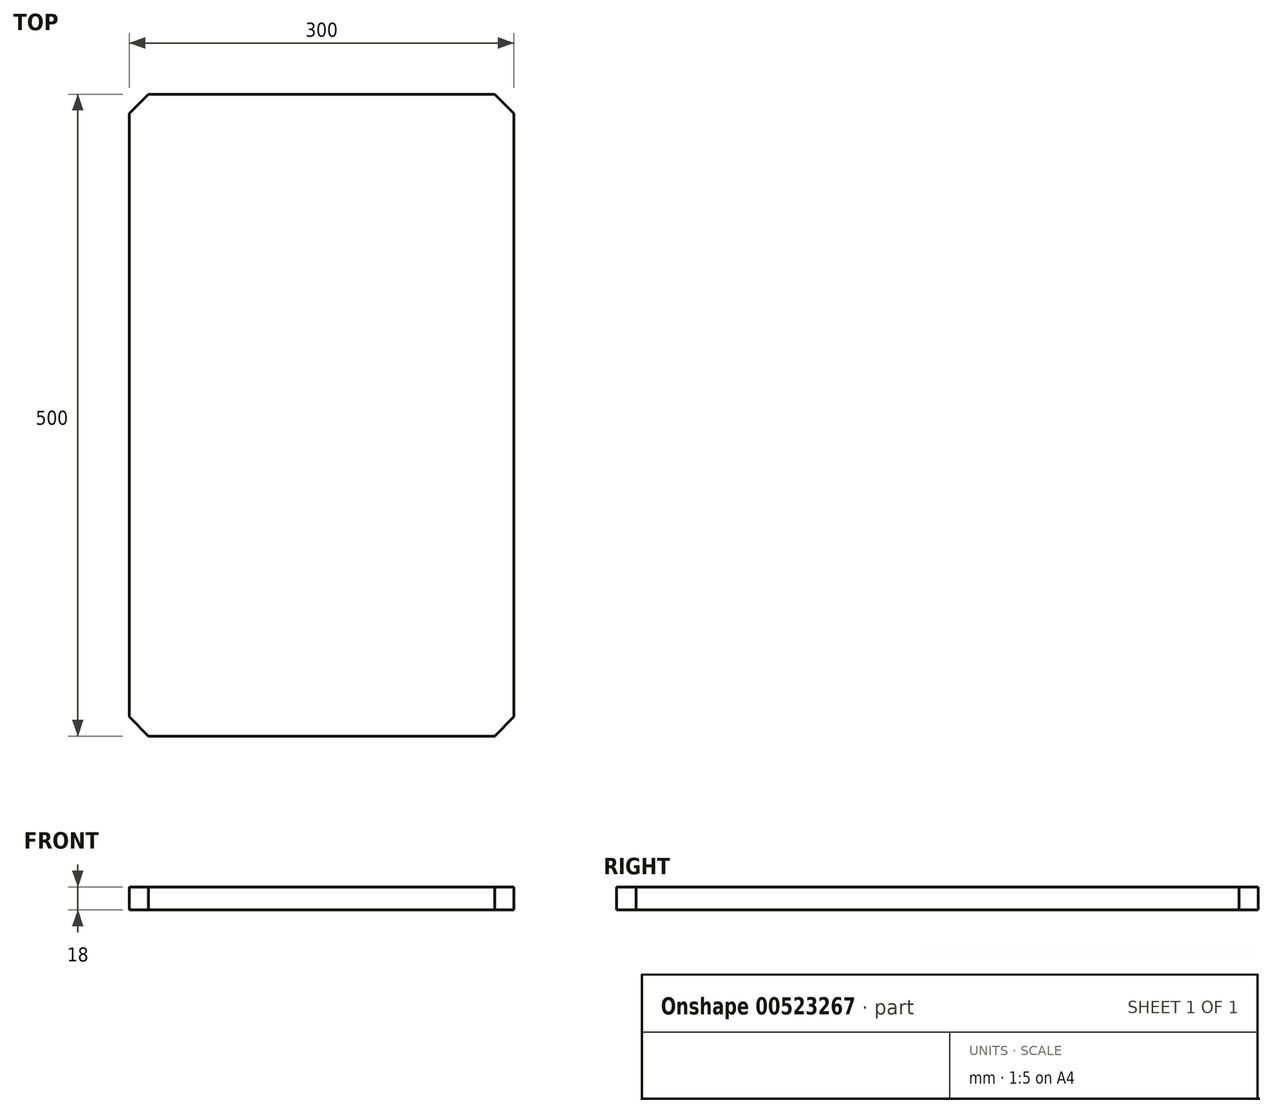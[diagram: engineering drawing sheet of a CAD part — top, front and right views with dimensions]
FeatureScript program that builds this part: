
annotation { "Feature Type Name" : "Feature", "Feature Type Description" : "" }
export const myFeature = defineFeature(function(context is Context, id is Id, definition is map)
    precondition{}
    {
        {
            var Q0;
            Q0=qCreatedBy(makeId("Top.planeOp"),FACE);
            var sketch = newSketch(context, id + "F0", { "sketchPlane" : qUnion([Q0])});
            skLineSegment(sketch, "E0.bottom", {"start": v(-107.73, -266.1) * mm, "end": v(192.27, -266.1) * mm});
            skLineSegment(sketch, "E0.top", {"start": v(-107.73, 233.9) * mm, "end": v(192.27, 233.9) * mm});
            skLineSegment(sketch, "E0.left", {"start": v(-107.73, -266.1) * mm, "end": v(-107.73, 233.9) * mm});
            skLineSegment(sketch, "E0.right", {"start": v(192.27, -266.1) * mm, "end": v(192.27, 233.9) * mm});
            skSolve(sketch);
        }
        {
            var Q0;
            Q0=makeQuery(id+"F0.imprint","IMPRINT",FACE,{"disambiguationData":[TD([[makeQuery(id+"F0.imprint","IMPRINT",EDGE,{"derivedFrom":sQuery(id+"F0.wireOp",EDGE,"E0.bottom")}),1.0]])]});
            extrude(context, id + "F1", {"entities" : qUnion([Q0]), "depth" : 18 * mm, "offsetDistance" : 25 * mm});
        }
        {
            var Q0;
            Q0=makeQuery(id+"F1.opExtrude","SWEPT_EDGE",EDGE,{"disambiguationData":[OSD([sQuery(id+"F0.wireOp",EDGE,"E0.bottom"),sQuery(id+"F0.wireOp",EDGE,"E0.right")])]});
            var Q1;
            Q1=makeQuery(id+"F1.opExtrude","SWEPT_EDGE",EDGE,{"disambiguationData":[OSD([sQuery(id+"F0.wireOp",EDGE,"E0.bottom"),sQuery(id+"F0.wireOp",EDGE,"E0.left")])]});
            var Q2;
            Q2=makeQuery(id+"F1.opExtrude","SWEPT_EDGE",EDGE,{"disambiguationData":[OSD([sQuery(id+"F0.wireOp",EDGE,"E0.top"),sQuery(id+"F0.wireOp",EDGE,"E0.right")])]});
            var Q3;
            Q3=makeQuery(id+"F1.opExtrude","SWEPT_EDGE",EDGE,{"disambiguationData":[OSD([sQuery(id+"F0.wireOp",EDGE,"E0.top"),sQuery(id+"F0.wireOp",EDGE,"E0.left")])]});
            chamfer(context, id + "F2", {"entities" : qUnion([Q0, Q1, Q2, Q3]), "width" : 15 * mm, "tangentPropagation" : true});
        }
    });
